# Revit family: Eyewash-Bradley_Corp-S19274JD
name_source: partatom
category: Plumbing Fixtures
revit_build: Autodesk Revit 2013 (Build: 20120221_2030(x64)
units: mm (PartAtom-declared; Revit-internal decimal feet)

## types (1)
- S19274JD
    Assembly Code = D2010710
    Barrier-Free = No
    Buy American Act = TBD
    CWFU = 0
    Cold Water Connection Diameter = 1"
    Cold Water Connection Radius = 0"
    Default Elevation = 36"
    Description = Deck-Mount Swing-Down Halo Eye/Face Wash Unit
    Eyewash On = Yes
    Fixture Material = Metal - Bradley Corp - Chrome
    Height = 7"
    Industry Standards = ANSI Z358.1-2009, cUPC
    Length = 11"
    Manufacturer = Bradley Corporation
    Manufacturer Installation URL - English = https://www.bradleycorp.com
    MasterFormat Number = 22.45.26
    MasterFormat Title = Eye/Face Wash Equipment
    Model = S19274JD
    Mounting Height = 0"
    Navigator EFX8 Emergency Thermostatic Mixing Valve = No
    On Position = Yes
    Percentage of Recycled Content = 0
    Pipe Fitting Material = Metal - Bradley Corp - Chrome
    Product Page URL = https://www.bradleycorp.com
    Product Tech Data URL - English = https://www.bradleycorp.com
    Product Tech Data URL - Spanish = https://www.bradleycorp.com
    Specifications URL = https://www.bradleycorp.com
    URL = http://www.bradleycorp.com
    Version = 1.0
    WFU = 0
    Warranty Information = Full, One-Year Warranty
    Waste Connection Radius = 1"
    Width = 7 5/8"

## geometry (parser evidence)
native form markers: Blend x14, Sweep x5
no freeform markers — native parametric forms only
